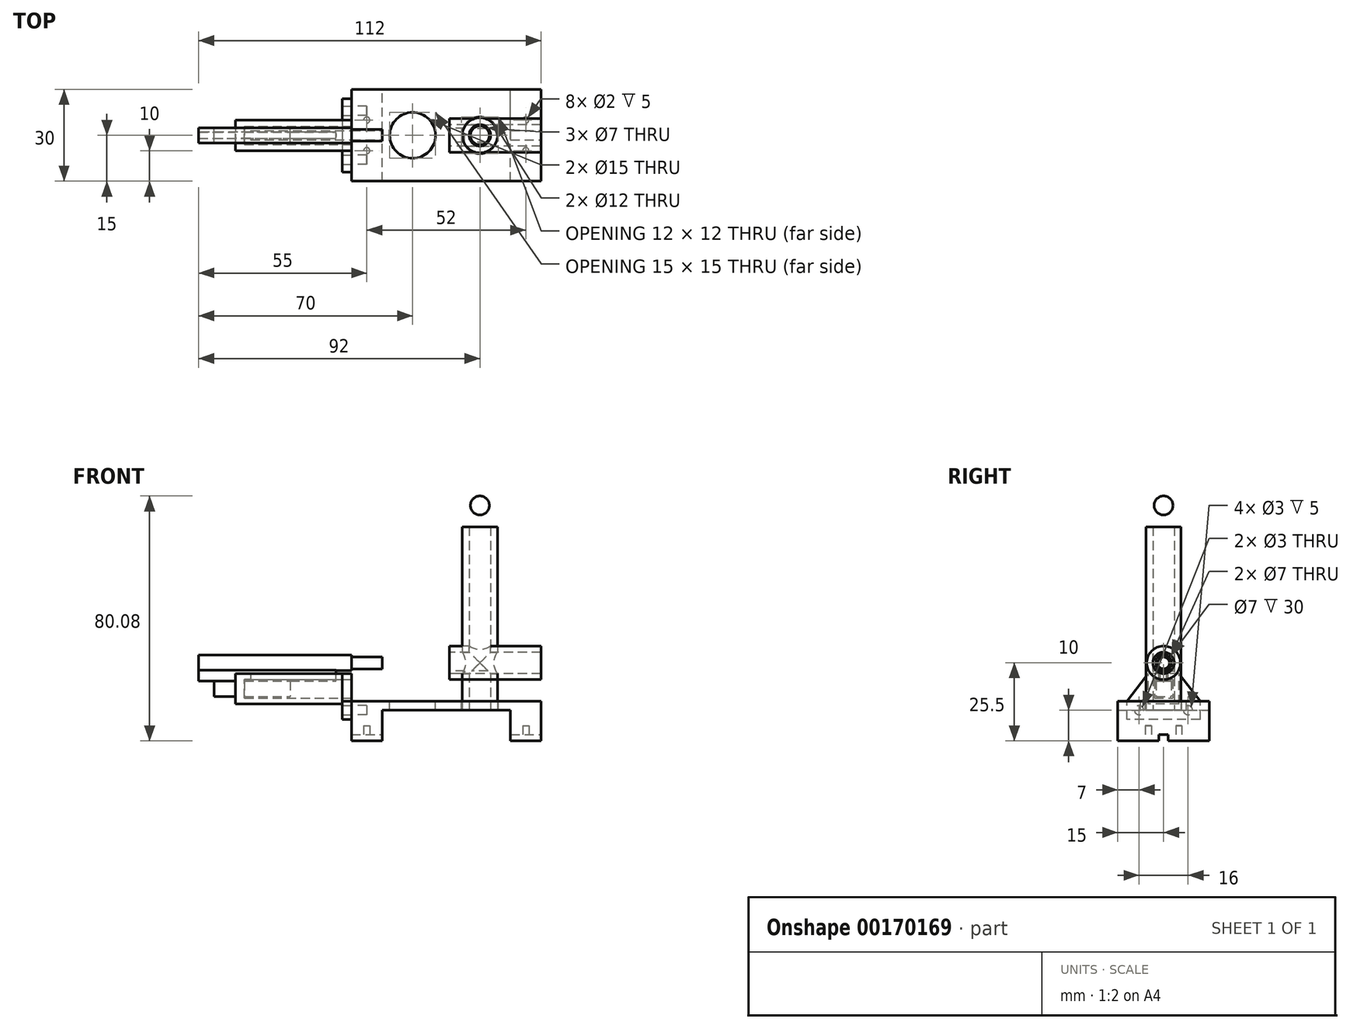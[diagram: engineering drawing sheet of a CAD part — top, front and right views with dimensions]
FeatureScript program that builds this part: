
annotation { "Feature Type Name" : "Feature", "Feature Type Description" : "" }
export const myFeature = defineFeature(function(context is Context, id is Id, definition is map)
    precondition{}
    {
        {
            var Q0;
            Q0=qCreatedBy(makeId("Front.planeOp"),FACE);
            var sketch = newSketch(context, id + "F0", { "sketchPlane" : qUnion([Q0])});
            skLineSegment(sketch, "E0", {"start": v(-31, -10) * mm, "end": v(-31, 3) * mm});
            skLineSegment(sketch, "E1", {"start": v(-31, 3) * mm, "end": v(31, 3) * mm});
            skLineSegment(sketch, "E2", {"start": v(31, 3) * mm, "end": v(31, -10) * mm});
            skLineSegment(sketch, "E3", {"start": v(31, -10) * mm, "end": v(21, -10) * mm});
            skLineSegment(sketch, "E4", {"start": v(21, -10) * mm, "end": v(21, 0) * mm});
            skLineSegment(sketch, "E5", {"start": v(21, 0) * mm, "end": v(-21, 0) * mm});
            skLineSegment(sketch, "E6", {"start": v(-21, 0) * mm, "end": v(-21, -10) * mm});
            skLineSegment(sketch, "E7", {"start": v(-21, -10) * mm, "end": v(-31, -10) * mm});
            skSolve(sketch);
        }
        {
            var Q0;
            Q0=makeQuery(id+"F0.imprint","IMPRINT",FACE,{"disambiguationData":[TD([[makeQuery(id+"F0.imprint","IMPRINT",EDGE,{"derivedFrom":sQuery(id+"F0.wireOp",EDGE,"E0")}),-1.0]])]});
            extrude(context, id + "F1", {"entities" : qUnion([Q0]), "depth" : 30 * mm, "symmetric" : true});
        }
        {
            var Q0;
            Q0=makeQuery(id+"F1.opExtrude","SWEPT_FACE",FACE,{"disambiguationData":[OSD([sQuery(id+"F0.wireOp",EDGE,"E7")])]});
            var sketch = newSketch(context, id + "F2", { "sketchPlane" : qUnion([Q0])});
            skLineSegment(sketch, "E8.bottom", {"start": v(-31, 1.5) * mm, "end": v(36.21, 1.5) * mm});
            skLineSegment(sketch, "E8.top", {"start": v(-31, -1.5) * mm, "end": v(36.21, -1.5) * mm});
            skLineSegment(sketch, "E8.left", {"start": v(-31, 1.5) * mm, "end": v(-31, -1.5) * mm});
            skLineSegment(sketch, "E8.right", {"start": v(36.21, 1.5) * mm, "end": v(36.21, -1.5) * mm});
            skSolve(sketch);
        }
        {
            var Q0;
            {var subQ0=sQuery(id+"F2.wireOp",EDGE,"E8.left");Q0=makeQuery(id+"F2.imprint","IMPRINT",FACE,{"disambiguationData":[TD([[makeQuery(id+"F2.imprint","IMPRINT",EDGE,{"derivedFrom":subQ0}),1.0]])]});}
            var Q1;
            {var subQ0=sQuery(id+"F2.wireOp",EDGE,"E8.right");Q1=makeQuery(id+"F2.imprint","IMPRINT",FACE,{"disambiguationData":[TD([[makeQuery(id+"F2.imprint","IMPRINT",EDGE,{"derivedFrom":subQ0}),-1.0]])]});}
            extrude(context, id + "F3", {"entities" : qUnion([Q0, Q1]), "operationType" : NewBodyOperationType.REMOVE, "oppositeDirection" : true, "depth" : 2 * mm});
        }
        {
            var Q0;
            {var subQ1=sQuery(id+"F0.wireOp",EDGE,"E7");Q0=makeQuery(id+"F3.boolean.opBoolean","SPLIT",FACE,{"disambiguationData":[TD([makeQuery(id+"F3.opExtrude","SWEPT_FACE",FACE,{"disambiguationData":[OSD([sQuery(id+"F2.wireOp",EDGE,"E8.bottom")])]})])],"derivedFrom":makeQuery(id+"F1.opExtrude","SWEPT_FACE",FACE,{"disambiguationData":[OSD([subQ1])]})});}
            var sketch = newSketch(context, id + "F4", { "sketchPlane" : qUnion([Q0])});
            skCircle(sketch, "E9", {"center": v(-26, 5) * mm, "radius": 1 * mm});
            skPoint(sketch, "E9.centerSnap0", {"position": v(-26, 1.5) * mm});
            skCircle(sketch, "E10", {"center": v(-26, -5) * mm, "radius": 1 * mm});
            skCircle(sketch, "E11", {"center": v(26, 5) * mm, "radius": 1 * mm});
            skCircle(sketch, "E12", {"center": v(26, -5) * mm, "radius": 1 * mm});
            skSolve(sketch);
        }
        {
            var Q0;
            Q0 = qSketchRegion(id + "F4", true);
            extrude(context, id + "F5", {"entities" : qUnion([Q0]), "operationType" : NewBodyOperationType.REMOVE, "oppositeDirection" : true, "depth" : 5 * mm});
        }
        {
            var Q0;
            Q0=makeQuery(id+"F1.opExtrude","SWEPT_FACE",FACE,{"disambiguationData":[OSD([sQuery(id+"F0.wireOp",EDGE,"E0")])]});
            var sketch = newSketch(context, id + "F6", { "sketchPlane" : qUnion([Q0])});
            skCircle(sketch, "E13", {"center": v(-8, 0) * mm, "radius": 1.5 * mm});
            skCircle(sketch, "E14", {"center": v(8, 0) * mm, "radius": 1.5 * mm});
            skSolve(sketch);
        }
        {
            var Q0;
            Q0 = qSketchRegion(id + "F6", true);
            extrude(context, id + "F7", {"entities" : qUnion([Q0]), "operationType" : NewBodyOperationType.REMOVE, "oppositeDirection" : true, "depth" : 5 * mm});
        }
        {
            var Q0;
            Q0=makeQuery(id+"F1.opExtrude","SWEPT_FACE",FACE,{"disambiguationData":[OSD([sQuery(id+"F0.wireOp",EDGE,"E0")])]});
            var sketch = newSketch(context, id + "F8", { "sketchPlane" : qUnion([Q0])});
            skLineSegment(sketch, "E15.bottom", {"start": v(-12, -3) * mm, "end": v(12, -3) * mm});
            skLineSegment(sketch, "E15.top", {"start": v(-12, 12) * mm, "end": v(12, 12) * mm});
            skLineSegment(sketch, "E15.left", {"start": v(-12, -3) * mm, "end": v(-12, 12) * mm});
            skLineSegment(sketch, "E15.right", {"start": v(12, -3) * mm, "end": v(12, 12) * mm});
            skLineSegment(sketch, "E16", {"start": v(-5, 12) * mm, "end": v(-12, 3) * mm});
            skPoint(sketch, "E16.endSnap0", {"position": v(-12, 4.5) * mm});
            skLineSegment(sketch, "E17", {"start": v(5, 12) * mm, "end": v(12, 3) * mm});
            skSolve(sketch);
        }
        {
            var Q0;
            {var subQ0=sQuery(id+"F8.wireOp",EDGE,"E16");Q0=makeQuery(id+"F8.imprint","IMPRINT",FACE,{"disambiguationData":[TD([[makeQuery(id+"F8.imprint","IMPRINT",EDGE,{"derivedFrom":subQ0}),1.0]])]});}
            var Q1;
            {var subQ1=sQuery(id+"F8.wireOp",EDGE,"E15.bottom");Q1=makeQuery(id+"F8.imprint","IMPRINT",FACE,{"disambiguationData":[TD([[makeQuery(id+"F8.imprint","IMPRINT",EDGE,{"derivedFrom":subQ1}),1.0]])]});}
            extrude(context, id + "F9", {"entities" : qUnion([Q0, Q1]), "depth" : 3 * mm});
        }
        {
            var Q0;
            Q0=makeQuery(id+"F9.opExtrude","CAP_FACE",FACE,{"disambiguationData":[OSD([sQuery(id+"F6.wireOp",EDGE,"E13"),sQuery(id+"F6.wireOp",EDGE,"E14"),sQuery(id+"F8.wireOp",EDGE,"E15.bottom"),sQuery(id+"F8.wireOp",EDGE,"E15.top"),sQuery(id+"F8.wireOp",EDGE,"E15.left"),sQuery(id+"F8.wireOp",EDGE,"E15.right")])],"isStart":false});
            var sketch = newSketch(context, id + "F10", { "sketchPlane" : qUnion([Q0])});
            skPoint(sketch, "E18.firstSnap0", {"position": v(-12, 0) * mm});
            skLineSegment(sketch, "E18.bottom", {"start": v(-5, 2) * mm, "end": v(5, 2) * mm});
            skLineSegment(sketch, "E18.top", {"start": v(-5, 12) * mm, "end": v(5, 12) * mm});
            skLineSegment(sketch, "E18.left", {"start": v(-5, 2) * mm, "end": v(-5, 12) * mm});
            skLineSegment(sketch, "E18.right", {"start": v(5, 2) * mm, "end": v(5, 12) * mm});
            skSolve(sketch);
        }
        {
            var Q0;
            Q0=makeQuery(id+"F10.imprint","IMPRINT",FACE,{"disambiguationData":[TD([[makeQuery(id+"F10.imprint","IMPRINT",EDGE,{"derivedFrom":sQuery(id+"F10.wireOp",EDGE,"E18.bottom")}),1.0]])]});
            extrude(context, id + "F11", {"entities" : qUnion([Q0]), "operationType" : NewBodyOperationType.ADD, "depth" : 35 * mm});
        }
        {
            var Q0;
            Q0=makeQuery(id+"F9.opExtrude","CAP_FACE",FACE,{"disambiguationData":[OSD([sQuery(id+"F6.wireOp",EDGE,"E13"),sQuery(id+"F6.wireOp",EDGE,"E14"),sQuery(id+"F8.wireOp",EDGE,"E15.bottom"),sQuery(id+"F8.wireOp",EDGE,"E15.top"),sQuery(id+"F8.wireOp",EDGE,"E15.left"),sQuery(id+"F8.wireOp",EDGE,"E15.right")])],"isStart":true});
            var sketch = newSketch(context, id + "F12", { "sketchPlane" : qUnion([Q0])});
            skLineSegment(sketch, "E19.bottom", {"start": v(-3, 10) * mm, "end": v(-1.5, 10) * mm});
            skLineSegment(sketch, "E19.top", {"start": v(-3, 4) * mm, "end": v(3, 4) * mm});
            skLineSegment(sketch, "E19.left", {"start": v(-3, 10) * mm, "end": v(-3, 4) * mm});
            skLineSegment(sketch, "E19.right", {"start": v(3, 10) * mm, "end": v(3, 4) * mm});
            skLineSegment(sketch, "E20", {"start": v(-1.5, 10) * mm, "end": v(-1.5, 12) * mm});
            skLineSegment(sketch, "E21", {"start": v(1.5, 10) * mm, "end": v(1.5, 12) * mm});
            skLineSegment(sketch, "E22.trimOffspring", {"start": v(1.5, 10) * mm, "end": v(3, 10) * mm});
            skSolve(sketch);
        }
        {
            var Q0;
            Q0=makeQuery(id+"F12.imprint","IMPRINT",FACE,{"disambiguationData":[TD([[makeQuery(id+"F12.imprint","IMPRINT",EDGE,{"derivedFrom":sQuery(id+"F12.wireOp",EDGE,"E19.bottom")}),-1.0]])]});
            extrude(context, id + "F13", {"entities" : qUnion([Q0]), "operationType" : NewBodyOperationType.REMOVE, "oppositeDirection" : true, "depth" : 42 * mm});
        }
        {
            var Q0;
            Q0=makeQuery(id+"F1.opExtrude","SWEPT_FACE",FACE,{"disambiguationData":[OSD([sQuery(id+"F0.wireOp",EDGE,"E1")])]});
            var sketch = newSketch(context, id + "F14", { "sketchPlane" : qUnion([Q0])});
            skCircle(sketch, "E23", {"center": v(-11, 0) * mm, "radius": 7.5 * mm});
            skSolve(sketch);
        }
        {
            var Q0;
            Q0=makeQuery(id+"F14.imprint","IMPRINT",FACE,{"disambiguationData":[TD([[makeQuery(id+"F14.imprint","IMPRINT",EDGE,{"derivedFrom":sQuery(id+"F14.wireOp",EDGE,"E23")}),1.0]])]});
            extrude(context, id + "F15", {"entities" : qUnion([Q0]), "operationType" : NewBodyOperationType.REMOVE, "endBound" : BoundingType.THROUGH_ALL, "oppositeDirection" : true, "depth" : 25 * mm});
        }
        {
            var Q0;
            Q0=makeQuery(id+"F1.opExtrude","SWEPT_FACE",FACE,{"disambiguationData":[OSD([sQuery(id+"F0.wireOp",EDGE,"E1")])]});
            var sketch = newSketch(context, id + "F16", { "sketchPlane" : qUnion([Q0])});
            skCircle(sketch, "E24", {"center": v(11, 0) * mm, "radius": 6 * mm});
            skSolve(sketch);
        }
        {
            var Q0;
            Q0=makeQuery(id+"F16.imprint","IMPRINT",FACE,{"disambiguationData":[TD([[makeQuery(id+"F16.imprint","IMPRINT",EDGE,{"derivedFrom":sQuery(id+"F16.wireOp",EDGE,"E24")}),1.0]])]});
            extrude(context, id + "F17", {"entities" : qUnion([Q0]), "operationType" : NewBodyOperationType.REMOVE, "endBound" : BoundingType.THROUGH_ALL, "oppositeDirection" : true, "depth" : 2.5 * mm});
        }
        {
            var Q0;
            Q0=makeQuery(id+"F9.opExtrude","CAP_FACE",FACE,{"disambiguationData":[OSD([sQuery(id+"F6.wireOp",EDGE,"E13"),sQuery(id+"F6.wireOp",EDGE,"E14"),sQuery(id+"F8.wireOp",EDGE,"E15.bottom"),sQuery(id+"F8.wireOp",EDGE,"E15.top"),sQuery(id+"F8.wireOp",EDGE,"E15.left"),sQuery(id+"F8.wireOp",EDGE,"E15.right"),sQuery(id+"F8.wireOp",EDGE,"E16"),sQuery(id+"F8.wireOp",EDGE,"E17")])],"isStart":true});
            var sketch = newSketch(context, id + "F18", { "sketchPlane" : qUnion([Q0])});
            skLineSegment(sketch, "E25.bottom", {"start": v(-2.5, 9.5) * mm, "end": v(2.5, 9.5) * mm});
            skLineSegment(sketch, "E25.top", {"start": v(-2.5, 4.5) * mm, "end": v(2.5, 4.5) * mm});
            skLineSegment(sketch, "E25.left", {"start": v(-2.5, 9.5) * mm, "end": v(-2.5, 4.5) * mm});
            skLineSegment(sketch, "E25.right", {"start": v(2.5, 9.5) * mm, "end": v(2.5, 4.5) * mm});
            skLineSegment(sketch, "E26.bottom", {"start": v(-2.5, 18) * mm, "end": v(2.5, 18) * mm});
            skLineSegment(sketch, "E26.top", {"start": v(-2.5, 13) * mm, "end": v(2.5, 13) * mm});
            skLineSegment(sketch, "E26.left", {"start": v(-2.5, 18) * mm, "end": v(-2.5, 13) * mm});
            skLineSegment(sketch, "E26.right", {"start": v(2.5, 18) * mm, "end": v(2.5, 13) * mm});
            skLineSegment(sketch, "E27", {"start": v(-1, 9.5) * mm, "end": v(-1, 13) * mm});
            skLineSegment(sketch, "E28", {"start": v(1, 9.5) * mm, "end": v(1, 13) * mm});
            skSolve(sketch);
        }
        {
            var Q0;
            Q0=makeQuery(id+"F1.opExtrude","SWEPT_FACE",FACE,{"disambiguationData":[OSD([sQuery(id+"F0.wireOp",EDGE,"E5")])]});
            var sketch = newSketch(context, id + "F19", { "sketchPlane" : qUnion([Q0])});
            skCircle(sketch, "E29", {"center": v(11, 0) * mm, "radius": 5.75 * mm});
            skCircle(sketch, "E30", {"center": v(11, 0) * mm, "radius": 3.5 * mm});
            skSolve(sketch);
        }
        {
            var Q0;
            Q0=makeQuery(id+"F19.imprint","IMPRINT",FACE,{"disambiguationData":[TD([[makeQuery(id+"F19.imprint","IMPRINT",EDGE,{"derivedFrom":sQuery(id+"F19.wireOp",EDGE,"E29")}),1.0]])]});
            extrude(context, id + "F20", {"entities" : qUnion([Q0]), "oppositeDirection" : true, "depth" : 60 * mm});
        }
        {
            var Q0;
            Q0=makeQuery(id+"F18.imprint","IMPRINT",FACE,{"disambiguationData":[TD([[makeQuery(id+"F18.imprint","IMPRINT",EDGE,{"derivedFrom":sQuery(id+"F18.wireOp",EDGE,"E26.bottom")}),-1.0]])]});
            var Q1;
            {var subQ0=sQuery(id+"F18.wireOp",EDGE,"E27");Q1=makeQuery(id+"F18.imprint","IMPRINT",FACE,{"disambiguationData":[TD([[makeQuery(id+"F18.imprint","IMPRINT",EDGE,{"derivedFrom":subQ0}),-1.0]])]});}
            var Q2;
            Q2=makeQuery(id+"F18.imprint","IMPRINT",FACE,{"disambiguationData":[TD([[makeQuery(id+"F18.imprint","IMPRINT",EDGE,{"derivedFrom":sQuery(id+"F18.wireOp",EDGE,"E25.top")}),1.0]])]});
            extrude(context, id + "F21", {"entities" : qUnion([Q0, Q1, Q2]), "oppositeDirection" : true, "depth" : 50 * mm, "hasSecondDirection" : true, "secondDirectionOppositeDirection" : false, "secondDirectionDepth" : 10 * mm});
        }
        {
            var Q0;
            Q0=makeQuery(id+"F21.opExtrude","CAP_FACE",FACE,{"disambiguationData":[OSD([sQuery(id+"F18.wireOp",EDGE,"E25.bottom"),sQuery(id+"F18.wireOp",EDGE,"E25.top"),sQuery(id+"F18.wireOp",EDGE,"E25.left"),sQuery(id+"F18.wireOp",EDGE,"E25.right"),sQuery(id+"F18.wireOp",EDGE,"E26.bottom"),sQuery(id+"F18.wireOp",EDGE,"E26.top"),sQuery(id+"F18.wireOp",EDGE,"E26.left"),sQuery(id+"F18.wireOp",EDGE,"E26.right"),sQuery(id+"F18.wireOp",EDGE,"E27"),sQuery(id+"F18.wireOp",EDGE,"E28")])],"isStart":false});
            var sketch = newSketch(context, id + "F22", { "sketchPlane" : qUnion([Q0])});
            skLineSegment(sketch, "E31.0.0", {"start": v(2.5, 18) * mm, "end": v(-2.5, 18) * mm});
            skLineSegment(sketch, "E31.0.1", {"start": v(-2.5, 18) * mm, "end": v(-2.5, 13) * mm});
            skLineSegment(sketch, "E31.0.2", {"start": v(-2.5, 13) * mm, "end": v(-1, 13) * mm});
            skLineSegment(sketch, "E31.0.3", {"start": v(-1, 13) * mm, "end": v(-1, 9.5) * mm});
            skLineSegment(sketch, "E31.0.4", {"start": v(-1, 9.5) * mm, "end": v(-2.5, 9.5) * mm});
            skLineSegment(sketch, "E31.0.5", {"start": v(-2.5, 9.5) * mm, "end": v(-2.5, 4.5) * mm});
            skLineSegment(sketch, "E31.0.6", {"start": v(-2.5, 4.5) * mm, "end": v(2.5, 4.5) * mm});
            skLineSegment(sketch, "E31.0.7", {"start": v(2.5, 4.5) * mm, "end": v(2.5, 9.5) * mm});
            skLineSegment(sketch, "E31.0.8", {"start": v(2.5, 9.5) * mm, "end": v(1, 9.5) * mm});
            skLineSegment(sketch, "E31.0.9", {"start": v(1, 9.5) * mm, "end": v(1, 13) * mm});
            skLineSegment(sketch, "E31.0.10", {"start": v(1, 13) * mm, "end": v(2.5, 13) * mm});
            skLineSegment(sketch, "E31.0.11", {"start": v(2.5, 13) * mm, "end": v(2.5, 18) * mm});
            skLineSegment(sketch, "E32", {"start": v(1, 9.5) * mm, "end": v(-1, 9.5) * mm});
            skSolve(sketch);
        }
        {
            var Q0;
            Q0=makeQuery(id+"F22.imprint","IMPRINT",FACE,{"disambiguationData":[TD([[makeQuery(id+"F22.imprint","IMPRINT",EDGE,{"derivedFrom":sQuery(id+"F22.wireOp",EDGE,"E31.0.4")}),1.0]])]});
            extrude(context, id + "F23", {"entities" : qUnion([Q0]), "operationType" : NewBodyOperationType.REMOVE, "oppositeDirection" : true, "depth" : 5 * mm});
        }
        {
            var Q0;
            Q0=makeQuery(id+"F21.opExtrude","CAP_FACE",FACE,{"disambiguationData":[OSD([sQuery(id+"F18.wireOp",EDGE,"E25.bottom"),sQuery(id+"F18.wireOp",EDGE,"E25.top"),sQuery(id+"F18.wireOp",EDGE,"E25.left"),sQuery(id+"F18.wireOp",EDGE,"E25.right"),sQuery(id+"F18.wireOp",EDGE,"E26.bottom"),sQuery(id+"F18.wireOp",EDGE,"E26.top"),sQuery(id+"F18.wireOp",EDGE,"E26.left"),sQuery(id+"F18.wireOp",EDGE,"E26.right"),sQuery(id+"F18.wireOp",EDGE,"E27"),sQuery(id+"F18.wireOp",EDGE,"E28")])],"isStart":true});
            var sketch = newSketch(context, id + "F24", { "sketchPlane" : qUnion([Q0])});
            skLineSegment(sketch, "E33.0.0", {"start": v(2.5, 18) * mm, "end": v(-2.5, 18) * mm});
            skLineSegment(sketch, "E33.0.1", {"start": v(-2.5, 18) * mm, "end": v(-2.5, 13) * mm});
            skLineSegment(sketch, "E33.0.2", {"start": v(-2.5, 13) * mm, "end": v(-1, 13) * mm});
            skLineSegment(sketch, "E33.0.3", {"start": v(-1, 13) * mm, "end": v(-1, 9.5) * mm});
            skLineSegment(sketch, "E33.0.4", {"start": v(-1, 9.5) * mm, "end": v(-2.5, 9.5) * mm});
            skLineSegment(sketch, "E33.0.5", {"start": v(-2.5, 9.5) * mm, "end": v(-2.5, 4.5) * mm});
            skLineSegment(sketch, "E33.0.6", {"start": v(-2.5, 4.5) * mm, "end": v(2.5, 4.5) * mm});
            skLineSegment(sketch, "E33.0.7", {"start": v(2.5, 4.5) * mm, "end": v(2.5, 9.5) * mm});
            skLineSegment(sketch, "E33.0.8", {"start": v(2.5, 9.5) * mm, "end": v(1, 9.5) * mm});
            skLineSegment(sketch, "E33.0.9", {"start": v(1, 9.5) * mm, "end": v(1, 13) * mm});
            skLineSegment(sketch, "E33.0.10", {"start": v(1, 13) * mm, "end": v(2.5, 13) * mm});
            skLineSegment(sketch, "E33.0.11", {"start": v(2.5, 13) * mm, "end": v(2.5, 18) * mm});
            skLineSegment(sketch, "E34", {"start": v(1, 13) * mm, "end": v(-1, 13) * mm});
            skSolve(sketch);
        }
        {
            var Q0;
            Q0=makeQuery(id+"F24.imprint","IMPRINT",FACE,{"disambiguationData":[TD([[makeQuery(id+"F24.imprint","IMPRINT",EDGE,{"derivedFrom":sQuery(id+"F24.wireOp",EDGE,"E33.0.3")}),-1.0]])]});
            extrude(context, id + "F25", {"entities" : qUnion([Q0]), "operationType" : NewBodyOperationType.REMOVE, "oppositeDirection" : true, "depth" : 15 * mm});
        }
        {
            var Q0;
            Q0=makeQuery(id+"F25.boolean.opBoolean","COPY",FACE,{"derivedFrom":makeQuery(id+"F25.opExtrude","CAP_FACE",FACE,{"disambiguationData":[OSD([sQuery(id+"F24.wireOp",EDGE,"E33.0.3"),sQuery(id+"F24.wireOp",EDGE,"E33.0.4"),sQuery(id+"F24.wireOp",EDGE,"E33.0.5"),sQuery(id+"F24.wireOp",EDGE,"E33.0.6"),sQuery(id+"F24.wireOp",EDGE,"E33.0.7"),sQuery(id+"F24.wireOp",EDGE,"E33.0.8"),sQuery(id+"F24.wireOp",EDGE,"E33.0.9"),sQuery(id+"F24.wireOp",EDGE,"E34")])],"isStart":false})});
            var sketch = newSketch(context, id + "F26", { "sketchPlane" : qUnion([Q0])});
            skLineSegment(sketch, "E35.0.0", {"start": v(1, 9.5) * mm, "end": v(1, 13) * mm});
            skLineSegment(sketch, "E35.0.1", {"start": v(1, 13) * mm, "end": v(-1, 13) * mm});
            skLineSegment(sketch, "E35.0.2", {"start": v(-1, 13) * mm, "end": v(-1, 9.5) * mm});
            skLineSegment(sketch, "E35.0.3", {"start": v(-1, 9.5) * mm, "end": v(-2.5, 9.5) * mm});
            skLineSegment(sketch, "E35.0.4", {"start": v(-2.5, 9.5) * mm, "end": v(-2.5, 4.5) * mm});
            skLineSegment(sketch, "E35.0.5", {"start": v(-2.5, 4.5) * mm, "end": v(2.5, 4.5) * mm});
            skLineSegment(sketch, "E35.0.6", {"start": v(2.5, 4.5) * mm, "end": v(2.5, 9.5) * mm});
            skLineSegment(sketch, "E35.0.7", {"start": v(2.5, 9.5) * mm, "end": v(1, 9.5) * mm});
            skLineSegment(sketch, "E36", {"start": v(1, 9.5) * mm, "end": v(-1, 9.5) * mm});
            skSolve(sketch);
        }
        {
            var Q0;
            Q0=makeQuery(id+"F26.imprint","IMPRINT",FACE,{"disambiguationData":[TD([[makeQuery(id+"F26.imprint","IMPRINT",EDGE,{"derivedFrom":sQuery(id+"F26.wireOp",EDGE,"E35.0.3")}),-1.0]])]});
            extrude(context, id + "F27", {"entities" : qUnion([Q0]), "operationType" : NewBodyOperationType.REMOVE, "oppositeDirection" : true, "depth" : 15 * mm});
        }
        {
            var Q0;
            Q0=makeQuery(id+"F20.opExtrude","CAP_FACE",FACE,{"disambiguationData":[OSD([sQuery(id+"F19.wireOp",EDGE,"E29"),sQuery(id+"F19.wireOp",EDGE,"E30")])],"isStart":false});
            var sketch = newSketch(context, id + "F28", { "sketchPlane" : qUnion([Q0])});
            skLineSegment(sketch, "E37", {"start": v(11, 5.75) * mm, "end": v(11, -5.75) * mm});
            skSolve(sketch);
        }
        {
            var Q0;
            Q0=sQuery(id+"F28.wireOp",EDGE,"E37");
            cPlane(context, id + "F29", {"entities" : qUnion([Q0]), "cplaneType" : CPlaneType.LINE_ANGLE, "offset" : 25 * mm, "angle" : 90 * degree, "width" : 150 * mm, "height" : 150 * mm});
        }
        {
            var Q0;
            Q0=qCreatedBy(id+"F29.planeOp",FACE);
            var sketch = newSketch(context, id + "F30", { "sketchPlane" : qUnion([Q0])});
            skCircle(sketch, "E38", {"center": v(0, 15.5) * mm, "radius": 5.5 * mm});
            skCircle(sketch, "E39", {"center": v(0, 15.5) * mm, "radius": 3.5 * mm});
            skSolve(sketch);
        }
        {
            var Q0;
            Q0=makeQuery(id+"F30.imprint","IMPRINT",FACE,{"disambiguationData":[TD([[makeQuery(id+"F30.imprint","IMPRINT",EDGE,{"derivedFrom":sQuery(id+"F30.wireOp",EDGE,"E38")}),1.0]])]});
            extrude(context, id + "F31", {"entities" : qUnion([Q0]), "depth" : 20 * mm, "hasSecondDirection" : true, "secondDirectionOppositeDirection" : true, "secondDirectionDepth" : 10 * mm});
        }
        {
            var Q0;
            Q0=makeQuery(id+"F31.opExtrude","CAP_FACE",FACE,{"disambiguationData":[OSD([sQuery(id+"F30.wireOp",EDGE,"E38"),sQuery(id+"F30.wireOp",EDGE,"E39")])],"isStart":false});
            var sketch = newSketch(context, id + "F32", { "sketchPlane" : qUnion([Q0])});
            skCircle(sketch, "E40.0", {"center": v(0, 15.5) * mm, "radius": 3.5 * mm});
            skSolve(sketch);
        }
        {
            var Q0;
            Q0=makeQuery(id+"F32.imprint","IMPRINT",FACE,{"disambiguationData":[TD([[makeQuery(id+"F32.imprint","IMPRINT",EDGE,{"derivedFrom":sQuery(id+"F32.wireOp",EDGE,"E40.0")}),1.0]])]});
            extrude(context, id + "F33", {"entities" : qUnion([Q0]), "operationType" : NewBodyOperationType.REMOVE, "oppositeDirection" : true, "depth" : 32.7 * mm});
        }
        {
            var Q0;
            {var subQ0=sQuery(id+"F28.wireOp",EDGE,"E37");var subQ1=makeQuery(id+"F20.opExtrude","CAP_EDGE",EDGE,{"disambiguationData":[OSD([sQuery(id+"F19.wireOp",EDGE,"E30")])],"isStart":false});var subQ2=makeQuery(id+"F28.imprint","INTERSECT",VERTEX,{"disambiguationData":[OD(0.0)],"derivedFrom":[subQ1,subQ0]});Q0=makeQuery(id+"F28.imprint","IMPRINT",FACE,{"disambiguationData":[TD([[makeQuery(id+"F28.imprint","IMPRINT",EDGE,{"disambiguationData":[TD([[subQ2,-1.0]])],"derivedFrom":subQ0}),-1.0]])]});}
            var Q1;
            {var subQ0=sQuery(id+"F28.wireOp",EDGE,"E37");var subQ1=makeQuery(id+"F20.opExtrude","CAP_EDGE",EDGE,{"disambiguationData":[OSD([sQuery(id+"F19.wireOp",EDGE,"E30")])],"isStart":false});var subQ2=makeQuery(id+"F28.imprint","INTERSECT",VERTEX,{"disambiguationData":[OD(0.0)],"derivedFrom":[subQ1,subQ0]});Q1=makeQuery(id+"F28.imprint","IMPRINT",FACE,{"disambiguationData":[TD([[makeQuery(id+"F28.imprint","IMPRINT",EDGE,{"disambiguationData":[TD([[subQ2,-1.0]])],"derivedFrom":subQ0}),1.0]])]});}
            extrude(context, id + "F34", {"entities" : qUnion([Q0, Q1]), "operationType" : NewBodyOperationType.REMOVE, "oppositeDirection" : true, "depth" : 47.2 * mm});
        }
        {
            var Q0;
            Q0=makeQuery(id+"F31.opExtrude","CAP_FACE",FACE,{"disambiguationData":[OSD([sQuery(id+"F30.wireOp",EDGE,"E38"),sQuery(id+"F30.wireOp",EDGE,"E39")])],"isStart":true});
            var sketch = newSketch(context, id + "F35", { "sketchPlane" : qUnion([Q0])});
            skCircle(sketch, "E41.0", {"center": v(0, 15.5) * mm, "radius": 3.5 * mm});
            skLineSegment(sketch, "E42", {"start": v(2.27, 12.84) * mm, "end": v(-2.27, 12.84) * mm});
            skSolve(sketch);
        }
        {
            var Q0;
            {var subQ0=sQuery(id+"F35.wireOp",EDGE,"E42");Q0=makeQuery(id+"F35.imprint","IMPRINT",FACE,{"disambiguationData":[TD([[makeQuery(id+"F35.imprint","IMPRINT",EDGE,{"derivedFrom":subQ0}),1.0]])]});}
            extrude(context, id + "F36", {"entities" : qUnion([Q0]), "oppositeDirection" : true, "depth" : 5 * mm});
        }
        {
            var Q0;
            Q0=makeQuery(id+"F21.opExtrude","CAP_FACE",FACE,{"disambiguationData":[OSD([sQuery(id+"F18.wireOp",EDGE,"E25.bottom"),sQuery(id+"F18.wireOp",EDGE,"E25.top"),sQuery(id+"F18.wireOp",EDGE,"E25.left"),sQuery(id+"F18.wireOp",EDGE,"E25.right"),sQuery(id+"F18.wireOp",EDGE,"E26.bottom"),sQuery(id+"F18.wireOp",EDGE,"E26.top"),sQuery(id+"F18.wireOp",EDGE,"E26.left"),sQuery(id+"F18.wireOp",EDGE,"E26.right"),sQuery(id+"F18.wireOp",EDGE,"E27"),sQuery(id+"F18.wireOp",EDGE,"E28")])],"isStart":true});
            var sketch = newSketch(context, id + "F37", { "sketchPlane" : qUnion([Q0])});
            skCircle(sketch, "E43", {"center": v(0, 15.44) * mm, "radius": 1.94 * mm});
            skLineSegment(sketch, "E44.0.0", {"start": v(-2.5, 18) * mm, "end": v(-2.5, 13) * mm});
            skLineSegment(sketch, "E44.0.1", {"start": v(-2.5, 13) * mm, "end": v(2.5, 13) * mm});
            skLineSegment(sketch, "E44.0.2", {"start": v(2.5, 13) * mm, "end": v(2.5, 18) * mm});
            skLineSegment(sketch, "E44.0.3", {"start": v(2.5, 18) * mm, "end": v(-2.5, 18) * mm});
            skSolve(sketch);
        }
        {
            var Q0;
            Q0=makeQuery(id+"F37.imprint","IMPRINT",FACE,{"disambiguationData":[TD([[makeQuery(id+"F37.imprint","IMPRINT",EDGE,{"derivedFrom":sQuery(id+"F37.wireOp",EDGE,"E43")}),-1.0]])]});
            extrude(context, id + "F38", {"entities" : qUnion([Q0]), "operationType" : NewBodyOperationType.REMOVE, "oppositeDirection" : true, "depth" : 10 * mm});
        }
        {
            var Q0;
            Q0=qCreatedBy(id+"F29.planeOp",FACE);
            var sketch = newSketch(context, id + "F39", { "sketchPlane" : qUnion([Q0])});
            skArc(sketch, "E45", {"start": v(0, 63.88) * mm, "mid": v(3.1, 66.98) * mm, "end": v(0, 70.08) * mm});
            skLineSegment(sketch, "E46", {"start": v(0, 70.08) * mm, "end": v(0, 46.62) * mm});
            skSolve(sketch);
        }
        {
            var Q0;
            {var subQ0=sQuery(id+"F39.wireOp",EDGE,"E45");Q0=makeQuery(id+"F39.imprint","IMPRINT",FACE,{"disambiguationData":[TD([[makeQuery(id+"F39.imprint","IMPRINT",EDGE,{"derivedFrom":subQ0}),1.0]])]});}
            var Q1;
            Q1=sQuery(id+"F39.wireOp",EDGE,"E46");
            revolve(context, id + "F40", {"entities" : qUnion([Q0]), "axis" : qUnion([Q1]), "revolveType" : RevolveType.FULL});
        }
        {
            var Q0;
            Q0=makeQuery(id+"F11.opExtrude","CAP_FACE",FACE,{"disambiguationData":[OSD([sQuery(id+"F10.wireOp",EDGE,"E18.bottom"),sQuery(id+"F10.wireOp",EDGE,"E18.top"),sQuery(id+"F10.wireOp",EDGE,"E18.left"),sQuery(id+"F10.wireOp",EDGE,"E18.right")])],"isStart":false});
            var sketch = newSketch(context, id + "F41", { "sketchPlane" : qUnion([Q0])});
            skLineSegment(sketch, "E47.bottom", {"start": v(3, 4) * mm, "end": v(-3, 4) * mm});
            skLineSegment(sketch, "E47.top", {"start": v(3, 10) * mm, "end": v(-3, 10) * mm});
            skLineSegment(sketch, "E47.left", {"start": v(3, 4) * mm, "end": v(3, 10) * mm});
            skLineSegment(sketch, "E47.right", {"start": v(-3, 4) * mm, "end": v(-3, 10) * mm});
            skSolve(sketch);
        }
        {
            var Q0;
            Q0=makeQuery(id+"F41.imprint","IMPRINT",FACE,{"disambiguationData":[TD([[makeQuery(id+"F41.imprint","IMPRINT",EDGE,{"derivedFrom":sQuery(id+"F41.wireOp",EDGE,"E47.bottom")}),1.0]])]});
            extrude(context, id + "F42", {"entities" : qUnion([Q0]), "operationType" : NewBodyOperationType.ADD, "oppositeDirection" : true, "depth" : 3 * mm});
        }
        {
            var Q0;
            Q0=makeQuery(id+"F42.boolean.opBoolean","MERGE",FACE,{"derivedFrom":[makeQuery(id+"F11.opExtrude","CAP_FACE",FACE,{"disambiguationData":[OSD([sQuery(id+"F10.wireOp",EDGE,"E18.bottom"),sQuery(id+"F10.wireOp",EDGE,"E18.top"),sQuery(id+"F10.wireOp",EDGE,"E18.left"),sQuery(id+"F10.wireOp",EDGE,"E18.right")])],"isStart":false}),makeQuery(id+"F42.opExtrude","CAP_FACE",FACE,{"disambiguationData":[OSD([sQuery(id+"F41.wireOp",EDGE,"E47.bottom"),sQuery(id+"F41.wireOp",EDGE,"E47.top"),sQuery(id+"F41.wireOp",EDGE,"E47.left"),sQuery(id+"F41.wireOp",EDGE,"E47.right")])],"isStart":true})]});
            var sketch = newSketch(context, id + "F43", { "sketchPlane" : qUnion([Q0])});
            skLineSegment(sketch, "E48.bottom", {"start": v(-1.5, 12) * mm, "end": v(1.5, 12) * mm});
            skLineSegment(sketch, "E48.top", {"start": v(-1.5, 10) * mm, "end": v(1.5, 10) * mm});
            skLineSegment(sketch, "E48.left", {"start": v(-1.5, 12) * mm, "end": v(-1.5, 10) * mm});
            skLineSegment(sketch, "E48.right", {"start": v(1.5, 12) * mm, "end": v(1.5, 10) * mm});
            skSolve(sketch);
        }
        {
            var Q0;
            Q0=makeQuery(id+"F43.imprint","IMPRINT",FACE,{"disambiguationData":[TD([[makeQuery(id+"F43.imprint","IMPRINT",EDGE,{"derivedFrom":sQuery(id+"F43.wireOp",EDGE,"E48.bottom")}),-1.0]])]});
            extrude(context, id + "F44", {"entities" : qUnion([Q0]), "operationType" : NewBodyOperationType.ADD, "oppositeDirection" : true, "depth" : 5 * mm});
        }
        {
            var Q0;
            Q0=makeQuery(id+"F21.opExtrude","SWEPT_EDGE",EDGE,{"disambiguationData":[OSD([sQuery(id+"F18.wireOp",EDGE,"E26.bottom"),sQuery(id+"F18.wireOp",EDGE,"E26.left")])]});
            var Q1;
            Q1=makeQuery(id+"F21.opExtrude","SWEPT_EDGE",EDGE,{"disambiguationData":[OSD([sQuery(id+"F18.wireOp",EDGE,"E26.bottom"),sQuery(id+"F18.wireOp",EDGE,"E26.right")])]});
            var Q2;
            Q2=makeQuery(id+"F21.opExtrude","SWEPT_EDGE",EDGE,{"disambiguationData":[OSD([sQuery(id+"F18.wireOp",EDGE,"E26.top"),sQuery(id+"F18.wireOp",EDGE,"E26.left")])]});
            var Q3;
            Q3=makeQuery(id+"F21.opExtrude","SWEPT_EDGE",EDGE,{"disambiguationData":[OSD([sQuery(id+"F18.wireOp",EDGE,"E26.top"),sQuery(id+"F18.wireOp",EDGE,"E26.right")])]});
            fillet(context, id + "F45", {"entities" : qUnion([Q0, Q1, Q2, Q3]), "radius" : 2 * mm, "tangentPropagation" : true, "allowEdgeOverflow" : false});
        }
        {
            var Q0;
            Q0=makeQuery(id+"F1.opExtrude","SWEPT_BODY",BODY,{"disambiguationData":[OSD([sQuery(id+"F0.wireOp",EDGE,"E0"),sQuery(id+"F0.wireOp",EDGE,"E1"),sQuery(id+"F0.wireOp",EDGE,"E2"),sQuery(id+"F0.wireOp",EDGE,"E3"),sQuery(id+"F0.wireOp",EDGE,"E4"),sQuery(id+"F0.wireOp",EDGE,"E5"),sQuery(id+"F0.wireOp",EDGE,"E6"),sQuery(id+"F0.wireOp",EDGE,"E7")])]});
            transform(context, id + "F46", {"entities" : qUnion([Q0]), "transformType" : TransformType.TRANSLATION_3D, "dx" : 0 * mm, "dy" : 0 * mm, "dz" : 0 * mm, "makeCopy" : true});
        }
    });
